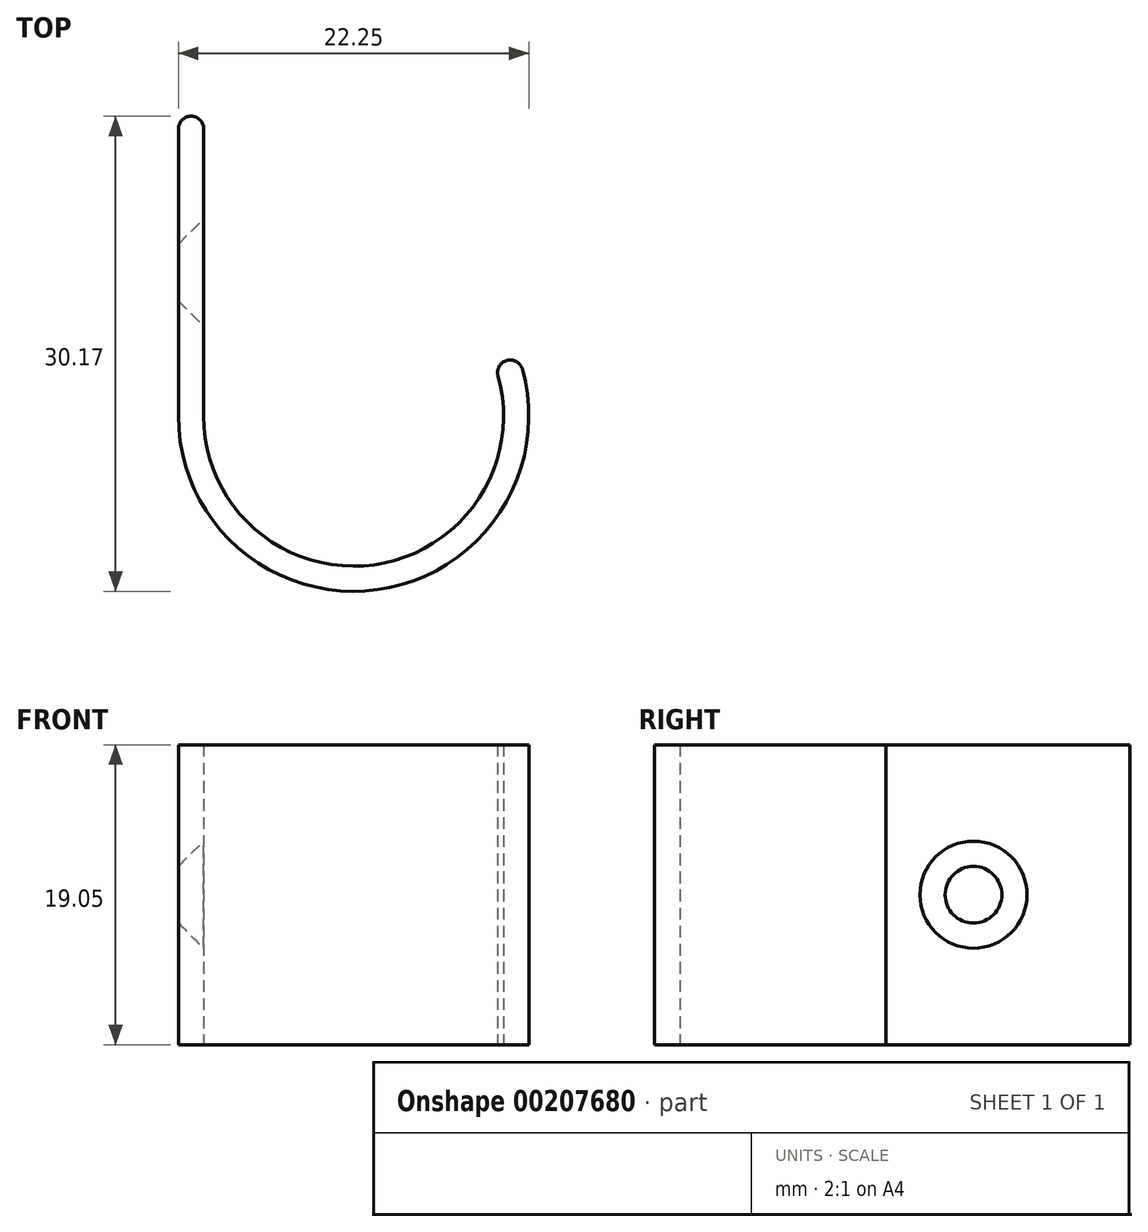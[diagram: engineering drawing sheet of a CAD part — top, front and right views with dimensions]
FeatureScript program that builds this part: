
annotation { "Feature Type Name" : "Feature", "Feature Type Description" : "" }
export const myFeature = defineFeature(function(context is Context, id is Id, definition is map)
    precondition{}
    {
        {
            var Q0;
            Q0=qCreatedBy(makeId("Top.planeOp"),FACE);
            var sketch = newSketch(context, id + "F0", { "sketchPlane" : qUnion([Q0])});
            skLineSegment(sketch, "E0", {"start": v(0, 0) * mm, "end": v(0, 18.25) * mm});
            skArc(sketch, "E1", {"start": v(0, 0) * mm, "mid": v(11.18, -9.38) * mm, "end": v(18.48, 3.26) * mm});
            skLineSegment(sketch, "E2.0", {"start": v(-1.6, 0) * mm, "end": v(-1.6, 18.25) * mm});
            skArc(sketch, "E2.1", {"start": v(-1.6, 0) * mm, "mid": v(11.46, -10.96) * mm, "end": v(19.98, 3.8) * mm});
            skLineSegment(sketch, "E3", {"start": v(-0.8, 19.05) * mm, "end": v(-0.8, 19.05) * mm});
            skPoint(sketch, "E4.visualSharp", {"position": v(0, 19.05) * mm});
            skArc(sketch, "E4.filletArc", {"start": v(0, 18.25) * mm, "mid": v(-0.23, 18.82) * mm, "end": v(-0.8, 19.05) * mm});
            skPoint(sketch, "E5.visualSharp", {"position": v(-1.6, 19.05) * mm});
            skArc(sketch, "E5.filletArc", {"start": v(-0.8, 19.05) * mm, "mid": v(-1.37, 18.82) * mm, "end": v(-1.6, 18.25) * mm});
            skLineSegment(sketch, "E6", {"start": v(18.48, 3.26) * mm, "end": v(19.98, 3.8) * mm});
            skLineSegment(sketch, "E7", {"start": v(0, 0) * mm, "end": v(9.53, 0) * mm, "construction": true});
            skLineSegment(sketch, "E8", {"start": v(9.53, 0) * mm, "end": v(18.48, 3.26) * mm, "construction": true});
            skSolve(sketch);
        }
        {
            var Q0;
            Q0 = qSketchRegion(id + "F0", true);
            extrude(context, id + "F1", {"entities" : qUnion([Q0]), "depth" : 19.05 * mm});
        }
        {
            var Q0;
            Q0=makeQuery(id+"F1.opExtrude","SWEPT_EDGE",EDGE,{"disambiguationData":[OSD([sQuery(id+"F0.wireOp",EDGE,"E2.1"),sQuery(id+"F0.wireOp",EDGE,"E6")])]});
            var Q1;
            Q1=makeQuery(id+"F1.opExtrude","SWEPT_EDGE",EDGE,{"disambiguationData":[OSD([sQuery(id+"F0.wireOp",EDGE,"E1"),sQuery(id+"F0.wireOp",EDGE,"E6")])]});
            fillet(context, id + "F2", {"entities" : qUnion([Q0, Q1]), "radius" : 0.8 * mm, "tangentPropagation" : true, "allowEdgeOverflow" : false});
        }
        {
            var Q0;
            Q0=makeQuery(id+"F1.opExtrude","SWEPT_FACE",FACE,{"disambiguationData":[OSD([sQuery(id+"F0.wireOp",EDGE,"E0")])]});
            var sketch = newSketch(context, id + "F3", { "sketchPlane" : qUnion([Q0])});
            skLineSegment(sketch, "E9", {"start": v(18.25, 9.53) * mm, "end": v(0, 9.53) * mm, "construction": true});
            skLineSegment(sketch, "E10", {"start": v(9.13, 19.05) * mm, "end": v(9.13, 0) * mm, "construction": true});
            skPoint(sketch, "E11", {"position": v(9.13, 9.53) * mm});
            skSolve(sketch);
        }
        {
            var Q0;
            Q0=sQuery(id+"F3.wireOp",VERTEX,"E11");
            var Q1;
            Q1=makeQuery(id+"F1.opExtrude","SWEPT_BODY",BODY,{"disambiguationData":[OSD([sQuery(id+"F0.wireOp",EDGE,"E0"),sQuery(id+"F0.wireOp",EDGE,"E1"),sQuery(id+"F0.wireOp",EDGE,"E2.0"),sQuery(id+"F0.wireOp",EDGE,"E2.1"),sQuery(id+"F0.wireOp",EDGE,"E4.filletArc"),sQuery(id+"F0.wireOp",EDGE,"E5.filletArc"),sQuery(id+"F0.wireOp",EDGE,"E6")])]});
            hole(context, id + "F4", {"style" : HoleStyle.C_SINK, "endStyle" : HoleEndStyle.THROUGH, "holeDiameter" : 3.4 * mm, "cSinkDiameter" : 6.8 * mm, "cSinkAngle" : 90 * degree, "locations" : qUnion([Q0]), "scope" : qUnion([Q1]), "isTappedThrough" : true});
        }
    });
